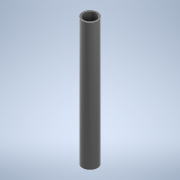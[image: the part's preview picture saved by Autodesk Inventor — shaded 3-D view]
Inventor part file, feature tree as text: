
AUTODESK INVENTOR PART (.ipt)
format: ipt  version: 2022 (Build 260153000, 153)  size: 100,352 bytes
history: native  units: in
note: dims shown in document units (in); Inventor stores cm internally (conversion verified against a paired STEP export)
features: sketch x2, extrude x1, hole x1
ambient origin geometry x8: Origin, YZ Plane, XZ Plane, XY Plane, X Axis, Y Axis, Z Axis, Center Point
bodies: Solid1 (feature_tree)
feature tree (4):
  extrude  "Extrusion1"  Depth=7.874in TaperAngle=0.0deg
  hole  "Hole3"  [1 undecoded]
  sketch  "Sketch1"  dims[d0=0.9449in d2=7.874in d3=0.0in]
  sketch  "Sketch5"  dims[d18=0.7874in d19=0.2362in d20=0.1575in d21=0.0787in d22=90.0deg d23=5.2799in d24=0.0in]
note: 1 required parameter value undecoded (feature->parameter linkage not recoverable at this tier; creation-order binding heuristic only, values carry confidence <= 0.55)
